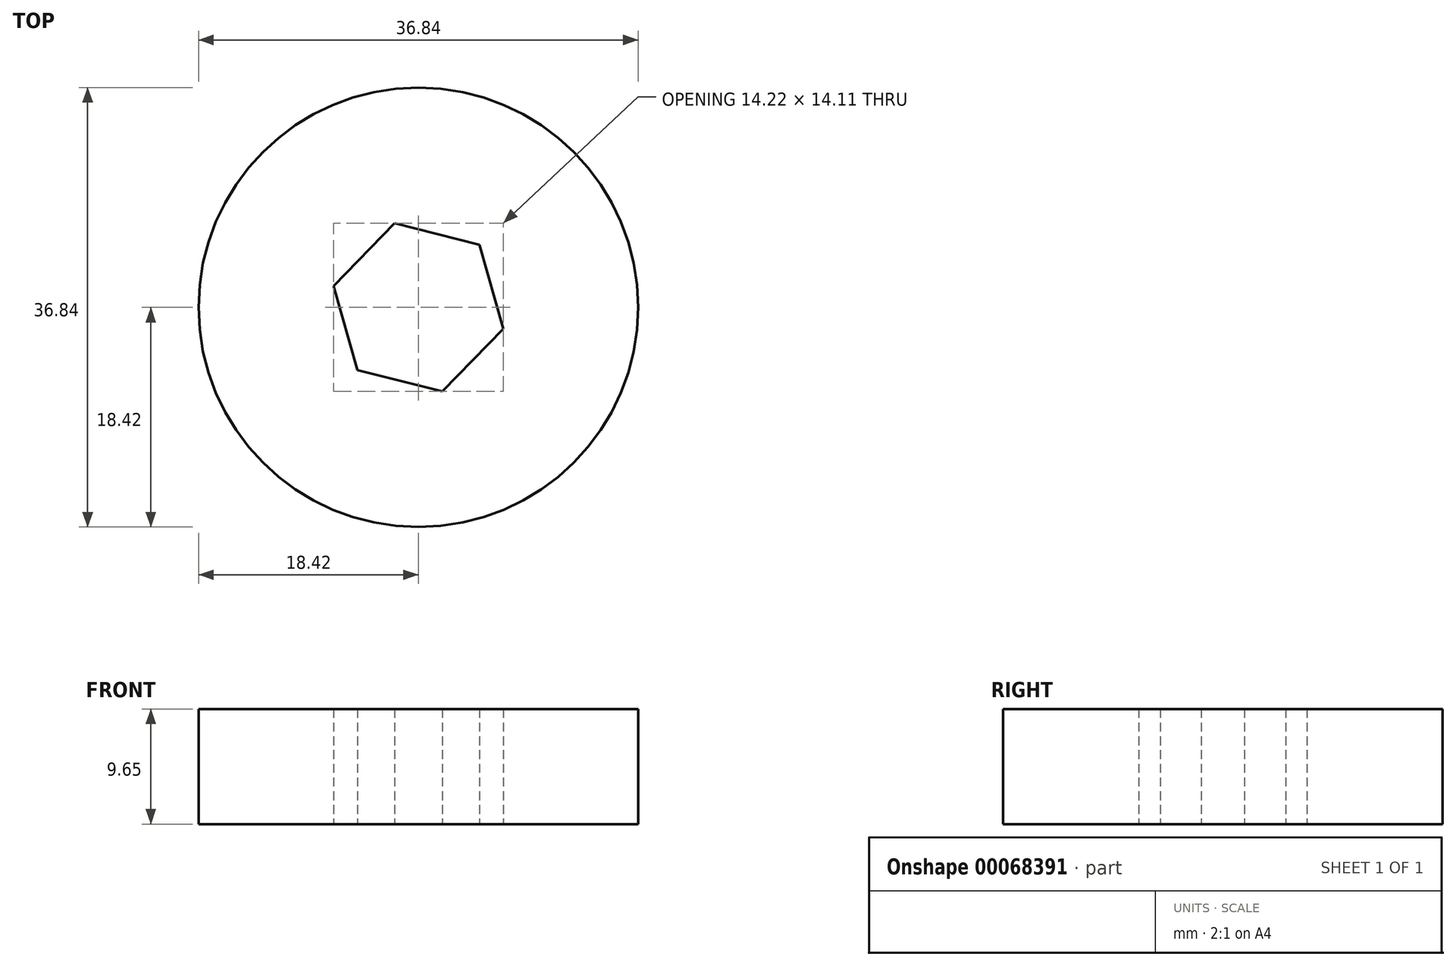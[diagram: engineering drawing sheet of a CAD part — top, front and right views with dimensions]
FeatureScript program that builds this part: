
annotation { "Feature Type Name" : "Feature", "Feature Type Description" : "" }
export const myFeature = defineFeature(function(context is Context, id is Id, definition is map)
    precondition{}
    {
        {
            var Q0;
            Q0=qCreatedBy(makeId("Top.planeOp"),FACE);
            var sketch = newSketch(context, id + "F0", { "sketchPlane" : qUnion([Q0])});
            skCircle(sketch, "E0.cCircle", {"center": v(0, 0) * mm, "radius": 6.35 * mm, "construction": true});
            skLineSegment(sketch, "E0.0", {"start": v(7.1, -1.8) * mm, "end": v(2, -7.06) * mm});
            skLineSegment(sketch, "E0.1", {"start": v(2, -7.06) * mm, "end": v(-5.11, -5.26) * mm});
            skLineSegment(sketch, "E0.2", {"start": v(-5.11, -5.26) * mm, "end": v(-7.1, 1.8) * mm});
            skLineSegment(sketch, "E0.3", {"start": v(-7.1, 1.8) * mm, "end": v(-2, 7.06) * mm});
            skLineSegment(sketch, "E0.4", {"start": v(-2, 7.06) * mm, "end": v(5.11, 5.26) * mm});
            skLineSegment(sketch, "E0.5", {"start": v(5.11, 5.26) * mm, "end": v(7.1, -1.8) * mm});
            skPoint(sketch, "E0.0.midPoint", {"position": v(4.55, -4.43) * mm});
            skCircle(sketch, "E1", {"center": v(0, 0) * mm, "radius": 18.41 * mm});
            skSolve(sketch);
        }
        {
            var Q0;
            Q0 = qSketchRegion(id + "F0", true);
            extrude(context, id + "F1", {"entities" : qUnion([Q0]), "depth" : 9.65 * mm});
        }
    });
